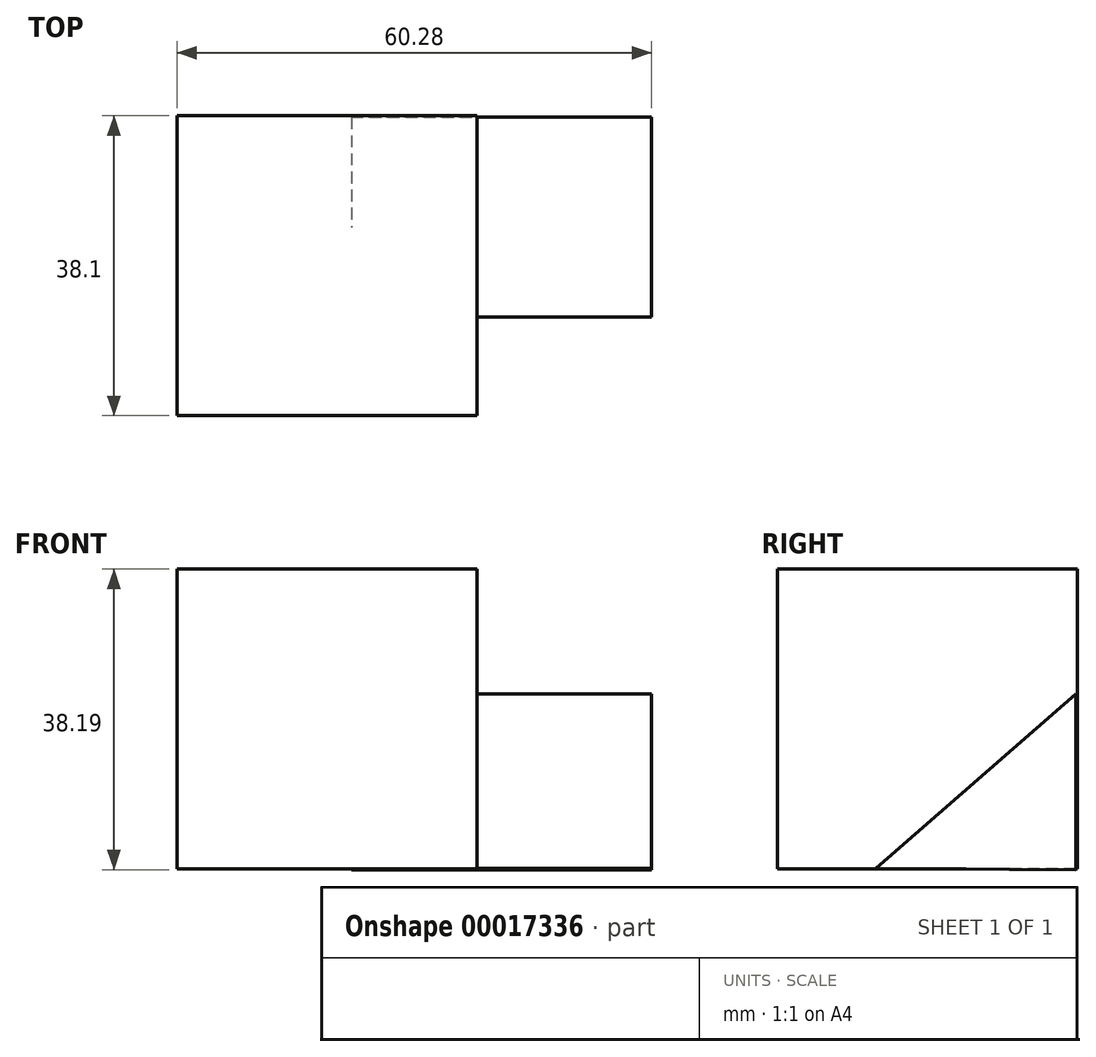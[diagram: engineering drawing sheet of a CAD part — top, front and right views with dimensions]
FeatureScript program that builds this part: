
annotation { "Feature Type Name" : "Feature", "Feature Type Description" : "" }
export const myFeature = defineFeature(function(context is Context, id is Id, definition is map)
    precondition{}
    {
        {
            var Q0;
            Q0=qCreatedBy(makeId("Front.planeOp"),FACE);
            var sketch = newSketch(context, id + "F0", { "sketchPlane" : qUnion([Q0])});
            skLineSegment(sketch, "E0.bottom", {"start": v(-22.18, 15.88) * mm, "end": v(15.92, 15.88) * mm});
            skLineSegment(sketch, "E0.top", {"start": v(-22.18, -22.22) * mm, "end": v(15.92, -22.22) * mm});
            skLineSegment(sketch, "E0.left", {"start": v(-22.18, 15.88) * mm, "end": v(-22.18, -22.22) * mm});
            skLineSegment(sketch, "E0.right", {"start": v(15.92, 15.88) * mm, "end": v(15.92, -22.22) * mm});
            skSolve(sketch);
        }
        {
            var Q0;
            Q0=makeQuery(id+"F0.imprint","IMPRINT",FACE,{"disambiguationData":[TD([[makeQuery(id+"F0.imprint","IMPRINT",EDGE,{"derivedFrom":sQuery(id+"F0.wireOp",EDGE,"E0.bottom")}),-1.0]])]});
            extrude(context, id + "F1", {"entities" : qUnion([Q0]), "oppositeDirection" : true, "depth" : 38.1 * mm});
        }
        {
            var Q0;
            Q0=qCreatedBy(makeId("Right.planeOp"),FACE);
            var sketch = newSketch(context, id + "F2", { "sketchPlane" : qUnion([Q0])});
            skLineSegment(sketch, "E1", {"start": v(12.5, -22.16) * mm, "end": v(37.9, 0) * mm});
            skLineSegment(sketch, "E2", {"start": v(37.9, 0) * mm, "end": v(37.9, -22.3) * mm});
            skLineSegment(sketch, "E3", {"start": v(37.9, -22.3) * mm, "end": v(12.5, -22.16) * mm});
            skSolve(sketch);
        }
        {
            var Q0;
            Q0 = qSketchRegion(id + "F2", true);
            extrude(context, id + "F3", {"entities" : qUnion([Q0]), "operationType" : NewBodyOperationType.ADD, "depth" : 38.1 * mm});
        }
    });
